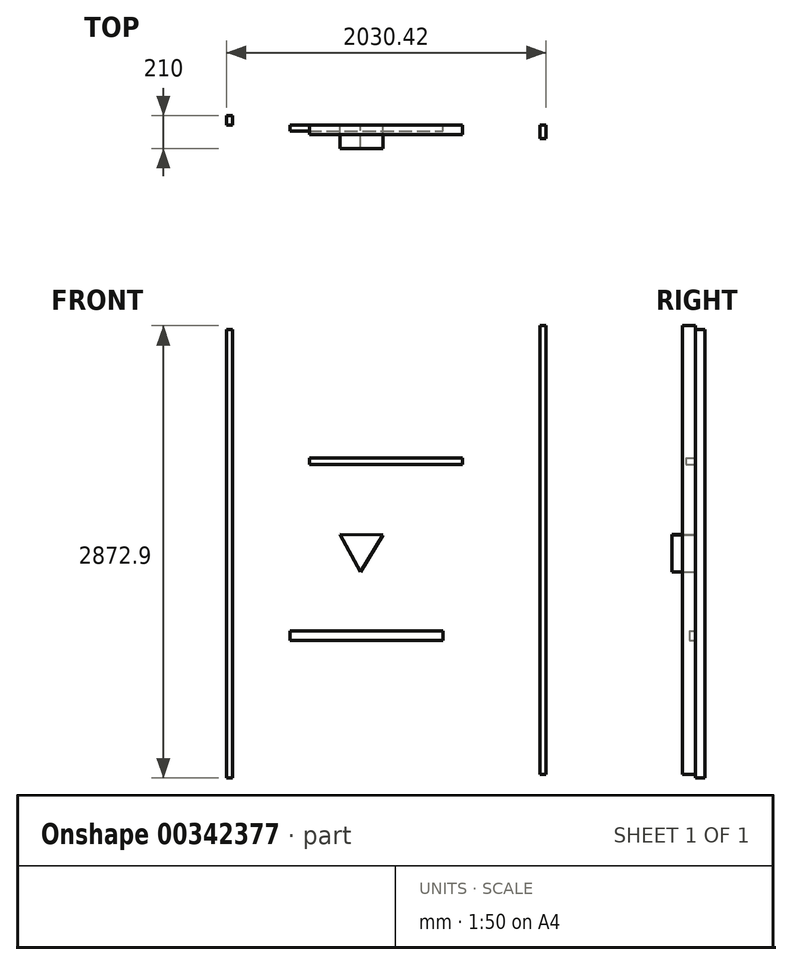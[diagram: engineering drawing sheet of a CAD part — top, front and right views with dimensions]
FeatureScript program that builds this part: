
annotation { "Feature Type Name" : "Feature", "Feature Type Description" : "" }
export const myFeature = defineFeature(function(context is Context, id is Id, definition is map)
    precondition{}
    {
        {
            var Q0;
            Q0=qCreatedBy(makeId("Front.planeOp"),FACE);
            var sketch = newSketch(context, id + "F0", { "sketchPlane" : qUnion([Q0])});
            skLineSegment(sketch, "E0.bottom", {"start": v(-893.5, -1428.25) * mm, "end": v(-853.5, -1428.25) * mm});
            skLineSegment(sketch, "E0.top", {"start": v(-893.5, 1421.75) * mm, "end": v(-853.5, 1421.75) * mm});
            skLineSegment(sketch, "E0.left", {"start": v(-893.5, -1428.25) * mm, "end": v(-893.5, 1421.75) * mm});
            skLineSegment(sketch, "E0.right", {"start": v(-853.5, -1428.25) * mm, "end": v(-853.5, 1421.75) * mm});
            skSolve(sketch);
        }
        {
            var Q0;
            Q0 = qSketchRegion(id + "F0", true);
            extrude(context, id + "F1", {"entities" : qUnion([Q0]), "oppositeDirection" : true, "depth" : 60 * mm});
        }
        {
            var Q0;
            Q0=qCreatedBy(makeId("Front.planeOp"),FACE);
            var sketch = newSketch(context, id + "F2", { "sketchPlane" : qUnion([Q0])});
            skLineSegment(sketch, "E1.bottom", {"start": v(605.74, 603.96) * mm, "end": v(-364.26, 603.96) * mm});
            skLineSegment(sketch, "E1.top", {"start": v(605.74, 563.96) * mm, "end": v(-364.26, 563.96) * mm});
            skLineSegment(sketch, "E1.left", {"start": v(605.74, 603.96) * mm, "end": v(605.74, 563.96) * mm});
            skLineSegment(sketch, "E1.right", {"start": v(-364.26, 603.96) * mm, "end": v(-364.26, 563.96) * mm});
            skSolve(sketch);
        }
        {
            var Q0;
            Q0 = qSketchRegion(id + "F2", true);
            extrude(context, id + "F3", {"entities" : qUnion([Q0]), "depth" : 60 * mm});
        }
        {
            var Q0;
            Q0=qCreatedBy(makeId("Front.planeOp"),FACE);
            var sketch = newSketch(context, id + "F4", { "sketchPlane" : qUnion([Q0])});
            skLineSegment(sketch, "E2.bottom", {"start": v(1136.92, 1444.65) * mm, "end": v(1096.92, 1444.65) * mm});
            skLineSegment(sketch, "E2.top", {"start": v(1136.92, -1405.35) * mm, "end": v(1096.92, -1405.35) * mm});
            skLineSegment(sketch, "E2.left", {"start": v(1136.92, 1444.65) * mm, "end": v(1136.92, -1405.35) * mm});
            skLineSegment(sketch, "E2.right", {"start": v(1096.92, 1444.65) * mm, "end": v(1096.92, -1405.35) * mm});
            skSolve(sketch);
        }
        {
            var Q0;
            Q0 = qSketchRegion(id + "F4", true);
            extrude(context, id + "F5", {"entities" : qUnion([Q0]), "depth" : 60 * mm});
        }
        {
            var Q0;
            Q0=qCreatedBy(makeId("Front.planeOp"),FACE);
            var sketch = newSketch(context, id + "F6", { "sketchPlane" : qUnion([Q0])});
            skLineSegment(sketch, "E3.bottom", {"start": v(-488.5, -493.23) * mm, "end": v(481.5, -493.23) * mm});
            skLineSegment(sketch, "E3.top", {"start": v(-488.5, -553.23) * mm, "end": v(481.5, -553.23) * mm});
            skLineSegment(sketch, "E3.left", {"start": v(-488.5, -493.23) * mm, "end": v(-488.5, -553.23) * mm});
            skLineSegment(sketch, "E3.right", {"start": v(481.5, -493.23) * mm, "end": v(481.5, -553.23) * mm});
            skSolve(sketch);
        }
        {
            var Q0;
            Q0 = qSketchRegion(id + "F6", true);
            extrude(context, id + "F7", {"entities" : qUnion([Q0]), "depth" : 40 * mm});
        }
        {
            var Q0;
            Q0=makeQuery(id+"F5.opExtrude","CAP_FACE",FACE,{"disambiguationData":[OSD([sQuery(id+"F4.wireOp",EDGE,"E2.bottom"),sQuery(id+"F4.wireOp",EDGE,"E2.top"),sQuery(id+"F4.wireOp",EDGE,"E2.left"),sQuery(id+"F4.wireOp",EDGE,"E2.right")])],"isStart":false});
            extrude(context, id + "F8", {"entities" : qUnion([Q0]), "operationType" : NewBodyOperationType.ADD, "depth" : 25 * mm});
        }
        {
            var Q0;
            Q0=qCreatedBy(makeId("Front.planeOp"),FACE);
            var sketch = newSketch(context, id + "F9", { "sketchPlane" : qUnion([Q0])});
            skCircle(sketch, "E4.cCircle", {"center": v(-37.5, 38.07) * mm, "radius": 78.97 * mm, "construction": true});
            skLineSegment(sketch, "E4.0", {"start": v(-40.75, -119.84) * mm, "end": v(-172.63, 119.84) * mm});
            skLineSegment(sketch, "E4.1", {"start": v(-172.63, 119.84) * mm, "end": v(100.87, 114.22) * mm});
            skLineSegment(sketch, "E4.2", {"start": v(100.87, 114.22) * mm, "end": v(-40.75, -119.84) * mm});
            skPoint(sketch, "E4.0.midPoint", {"position": v(-106.69, 0) * mm});
            skSolve(sketch);
        }
        {
            var Q0;
            Q0 = qSketchRegion(id + "F9", true);
            extrude(context, id + "F10", {"entities" : qUnion([Q0]), "depth" : 150 * mm});
        }
    });
